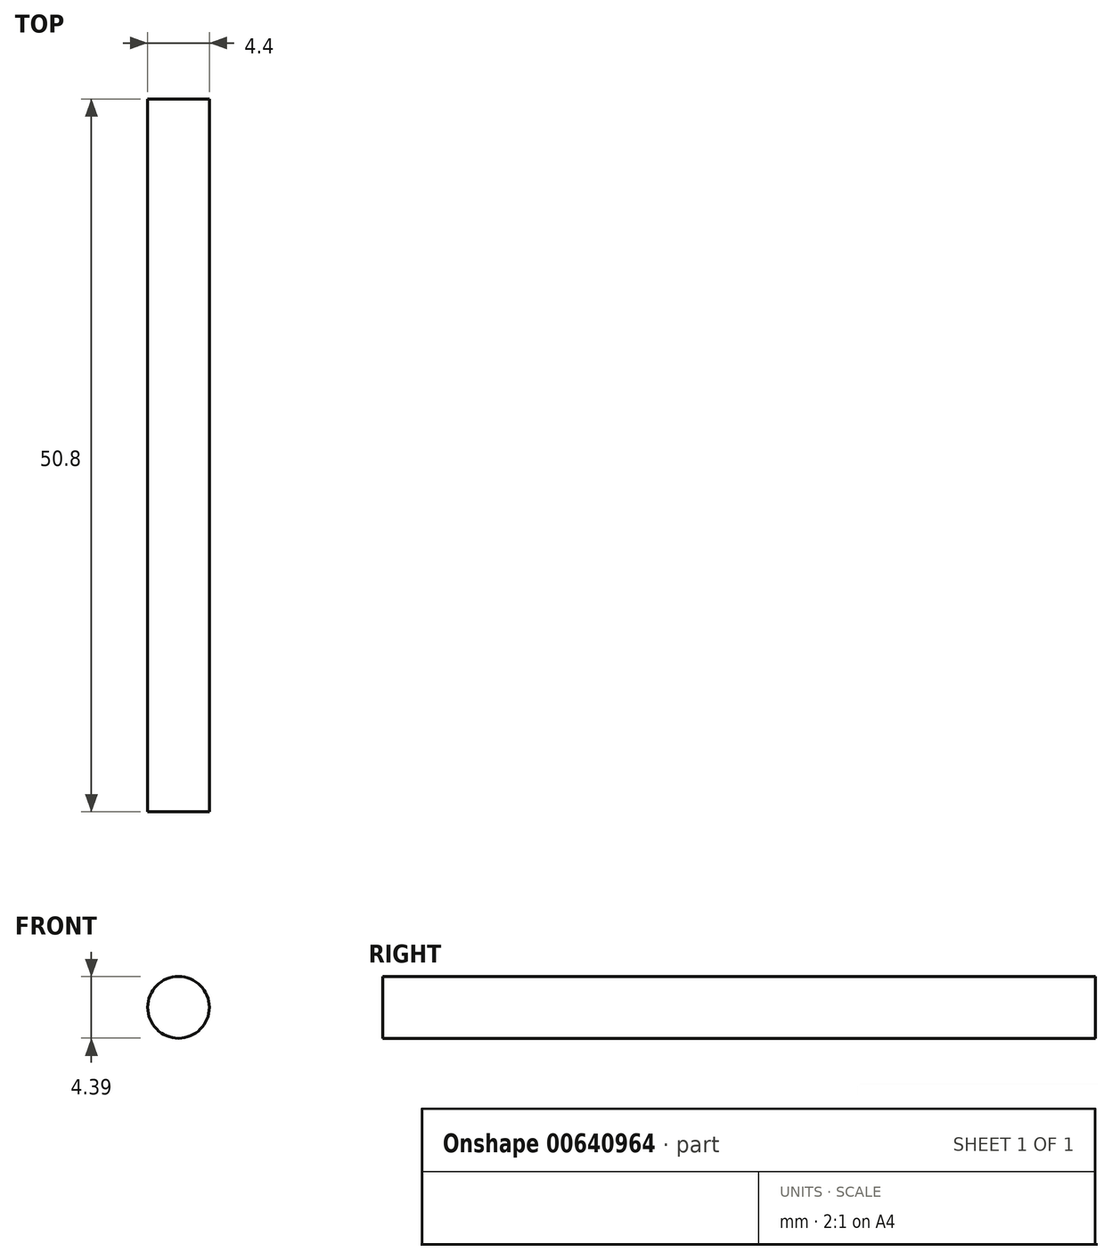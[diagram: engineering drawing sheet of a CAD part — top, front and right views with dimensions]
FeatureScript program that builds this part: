
annotation { "Feature Type Name" : "Feature", "Feature Type Description" : "" }
export const myFeature = defineFeature(function(context is Context, id is Id, definition is map)
    precondition{}
    {
        {
            var Q0;
            Q0=qCreatedBy(makeId("Front.planeOp"),FACE);
            var sketch = newSketch(context, id + "F0", { "sketchPlane" : qUnion([Q0])});
            skCircle(sketch, "E0", {"center": v(-65.02, 26.77) * mm, "radius": 2.2 * mm});
            skSolve(sketch);
        }
        {
            var Q0;
            Q0=makeQuery(id+"F0.imprint","IMPRINT",FACE,{"disambiguationData":[TD([[makeQuery(id+"F0.imprint","IMPRINT",EDGE,{"derivedFrom":sQuery(id+"F0.wireOp",EDGE,"E0")}),1.0]])]});
            extrude(context, id + "F1", {"entities" : qUnion([Q0]), "depth" : 50.8 * mm, "offsetDistance" : 25.4 * mm});
        }
    });
